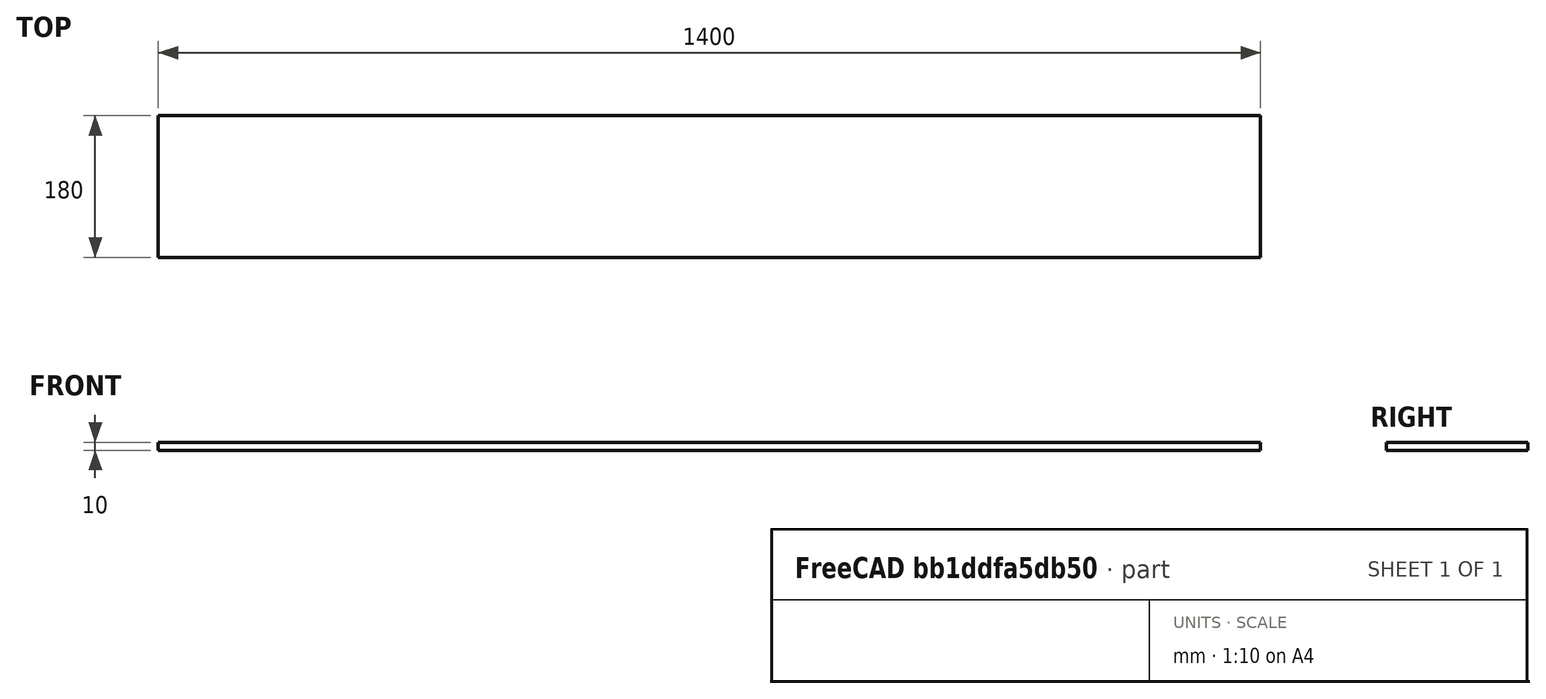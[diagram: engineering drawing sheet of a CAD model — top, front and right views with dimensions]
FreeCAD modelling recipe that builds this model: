
FCSTD DOCUMENT  (FreeCAD 0.19R24276 (Git))
Label: Place
License: All rights reserved
LicenseURL: http://en.wikipedia.org/wiki/All_rights_reserved
objects: Sketcher::SketchObject×1, PartDesign::Pad×1, PartDesign::Body×1
note: 4 computed .brp shape members not serialized (recipe doc carries the construction recipe); baked Part::Feature solids carry a one-line shape summary decoded from their .brp

FEATURE [Sketcher::SketchObject] Sketch
  FullyConstrained = true
  MapMode = 5
  Support = -> [XY_Plane]
  sketch-geometry (4):
    g0: LineSegment StartX=0 StartY=0 StartZ=0 EndX=1400 EndY=0 EndZ=0
    g1: LineSegment StartX=1400 StartY=0 StartZ=0 EndX=1400 EndY=180 EndZ=0
    g2: LineSegment StartX=1400 StartY=180 StartZ=0 EndX=0 EndY=180 EndZ=0
    g3: LineSegment StartX=0 StartY=180 StartZ=0 EndX=0 EndY=0 EndZ=0
  constraints (11):
    c: Coincident(g0,g1)
    c: Coincident(g1,g2)
    c: Coincident(g2,g3)
    c: Coincident(g3,g0)
    c: Horizontal(g0)
    c: Horizontal(g2)
    c: Vertical(g1)
    c: Vertical(g3)
    c: Coincident(g0,g-1)
    c: DistanceX(g0,g0) = 1400
    c: DistanceY(g3,g3) = 180
FEATURE [PartDesign::Pad] Pad
  Direction = (1,1,1)
  Length = 10
  Length2 = 100
  Profile = -> Sketch
  Type = 0
FEATURE [PartDesign::Body] Body
  Group = -> [Sketch,Pad]
  Origin = -> Origin
  Tip = -> Pad
